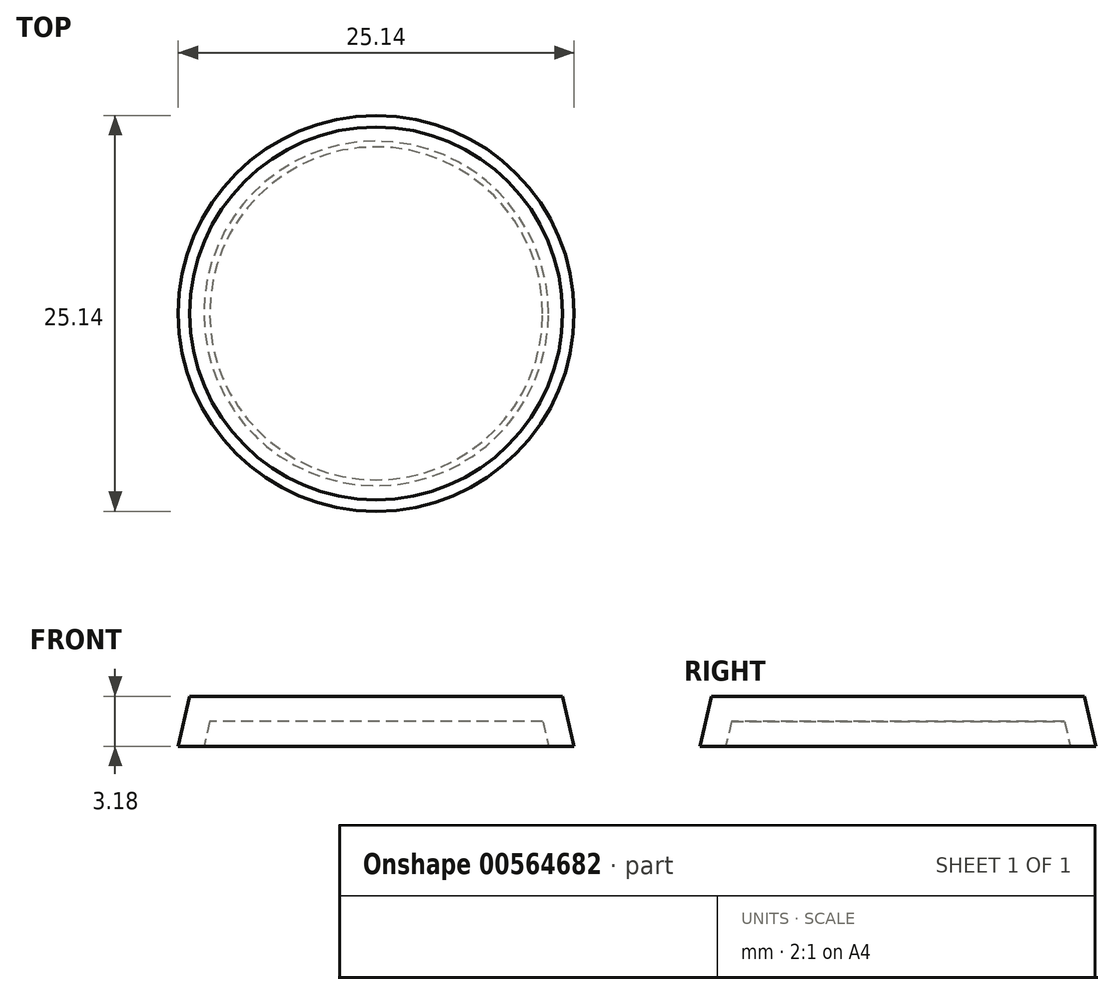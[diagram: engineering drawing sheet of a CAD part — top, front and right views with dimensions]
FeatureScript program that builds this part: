
annotation { "Feature Type Name" : "Feature", "Feature Type Description" : "" }
export const myFeature = defineFeature(function(context is Context, id is Id, definition is map)
    precondition{}
    {
        {
            var Q0;
            Q0=qCreatedBy(makeId("Top.planeOp"),FACE);
            var sketch = newSketch(context, id + "F0", { "sketchPlane" : qUnion([Q0])});
            skCircle(sketch, "E0", {"center": v(0, 0) * mm, "radius": 12.57 * mm});
            skSolve(sketch);
        }
        {
            var Q0;
            Q0=makeQuery(id+"F0.imprint","IMPRINT",FACE,{"disambiguationData":[TD([[makeQuery(id+"F0.imprint","IMPRINT",EDGE,{"derivedFrom":sQuery(id+"F0.wireOp",EDGE,"E0")}),1.0]])]});
            extrude(context, id + "F1", {"entities" : qUnion([Q0]), "depth" : 3.17 * mm, "offsetDistance" : 25.4 * mm, "hasDraft" : true, "draftAngle" : 13 * degree, "draftPullDirection" : true});
        }
        {
            var Q0;
            Q0=makeQuery(id+"F1.opExtrude","CAP_FACE",FACE,{"disambiguationData":[OSD([sQuery(id+"F0.wireOp",EDGE,"E0")])],"isStart":true});
            shell(context, id + "F2", {"entities" : qUnion([Q0]), "thickness" : 1.59 * mm});
        }
    });
